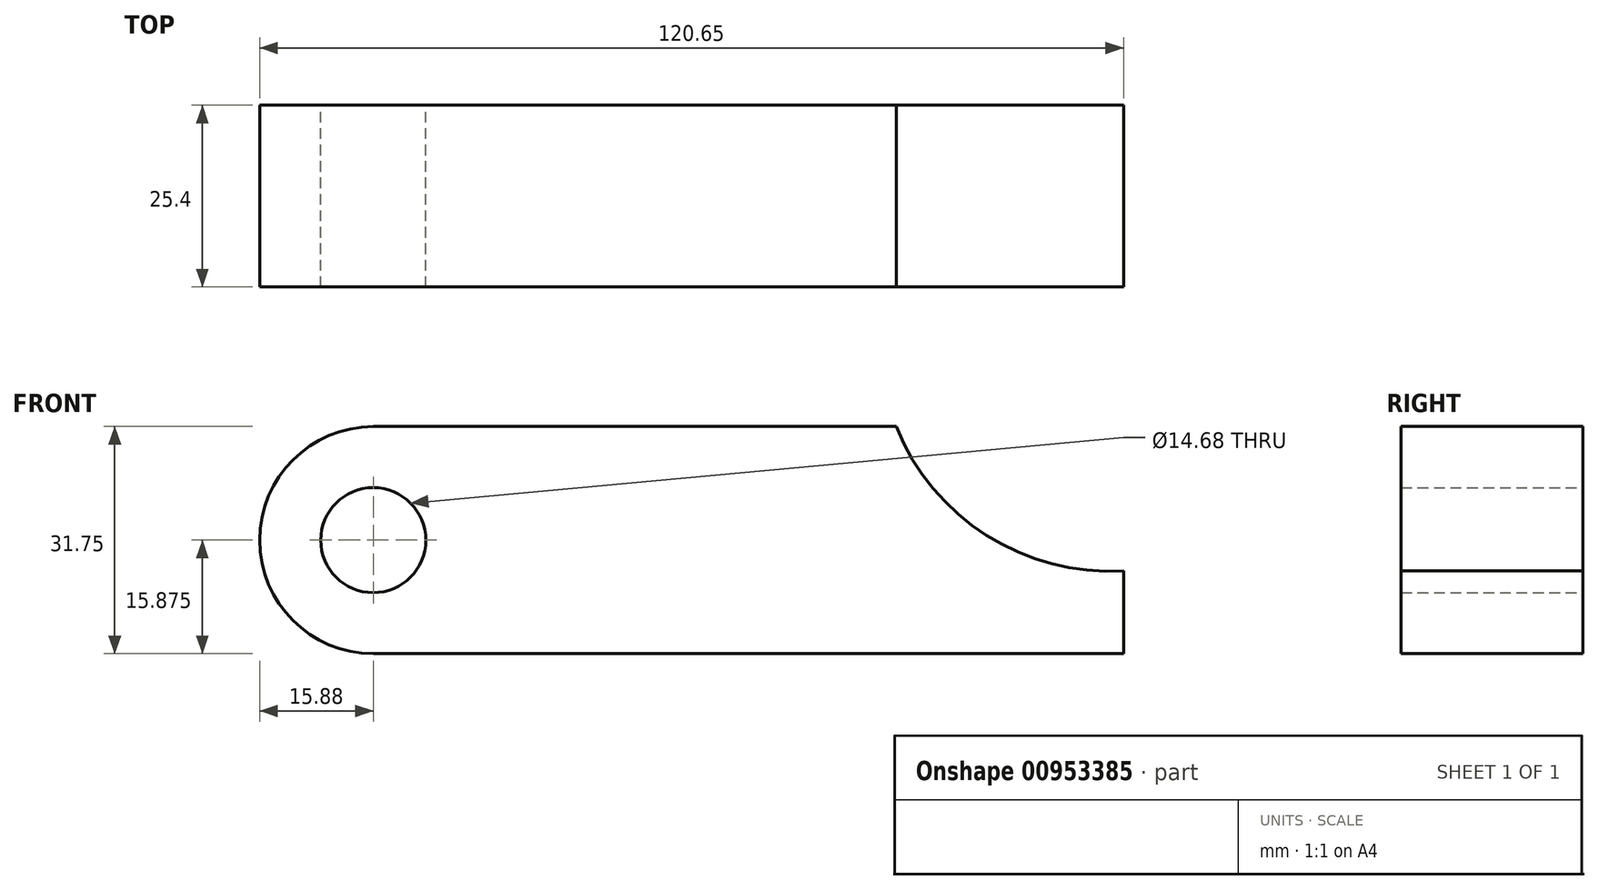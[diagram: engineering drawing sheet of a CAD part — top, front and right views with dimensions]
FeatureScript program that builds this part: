
annotation { "Feature Type Name" : "Feature", "Feature Type Description" : "" }
export const myFeature = defineFeature(function(context is Context, id is Id, definition is map)
    precondition{}
    {
        {
            var Q0;
            Q0=qCreatedBy(makeId("Front.planeOp"),FACE);
            var sketch = newSketch(context, id + "F0", { "sketchPlane" : qUnion([Q0])});
            skLineSegment(sketch, "E0", {"start": v(0, 0) * mm, "end": v(104.78, 0) * mm});
            skLineSegment(sketch, "E1", {"start": v(0, 0) * mm, "end": v(0, 31.75) * mm});
            skLineSegment(sketch, "E2", {"start": v(0, 31.75) * mm, "end": v(73.03, 31.75) * mm});
            skLineSegment(sketch, "E3", {"start": v(104.78, 11.57) * mm, "end": v(104.78, 0) * mm});
            skArc(sketch, "E4", {"start": v(73.03, 31.75) * mm, "mid": v(85.66, 16.56) * mm, "end": v(104.78, 11.57) * mm});
            skArc(sketch, "E5", {"start": v(0, 31.75) * mm, "mid": v(-15.87, 15.87) * mm, "end": v(0, 0) * mm});
            skCircle(sketch, "E6", {"center": v(0, 15.88) * mm, "radius": 7.34 * mm});
            skLineSegment(sketch, "E7", {"start": v(-15.87, 15.88) * mm, "end": v(14.9, 15.88) * mm});
            skSolve(sketch);
        }
        {
            var Q0;
            {var subQ5=sQuery(id+"F0.wireOp",EDGE,"E0");Q0=makeQuery(id+"F0.imprint","IMPRINT",FACE,{"disambiguationData":[TD([[makeQuery(id+"F0.imprint","IMPRINT",EDGE,{"derivedFrom":subQ5}),1.0]])]});}
            var Q1;
            {var subQ1=sQuery(id+"F0.wireOp",EDGE,"E1");var subQ3=sQuery(id+"F0.wireOp",EDGE,"E6");var subQ4=makeQuery(id+"F0.imprint","INTERSECT",VERTEX,{"disambiguationData":[OD(1.0)],"derivedFrom":[subQ1,subQ3]});Q1=makeQuery(id+"F0.imprint","IMPRINT",FACE,{"disambiguationData":[TD([[makeQuery(id+"F0.imprint","IMPRINT",EDGE,{"disambiguationData":[TD([[subQ4,-1.0]])],"derivedFrom":subQ3}),-1.0]])]});}
            var Q2;
            {var subQ1=sQuery(id+"F0.wireOp",EDGE,"E1");var subQ3=sQuery(id+"F0.wireOp",EDGE,"E6");var subQ4=makeQuery(id+"F0.imprint","INTERSECT",VERTEX,{"disambiguationData":[OD(0.0)],"derivedFrom":[subQ1,subQ3]});Q2=makeQuery(id+"F0.imprint","IMPRINT",FACE,{"disambiguationData":[TD([[makeQuery(id+"F0.imprint","IMPRINT",EDGE,{"disambiguationData":[TD([[subQ4,1.0]])],"derivedFrom":subQ3}),-1.0]])]});}
            extrude(context, id + "F1", {"entities" : qUnion([Q0, Q1, Q2]), "depth" : 25.4 * mm, "offsetDistance" : 25.4 * mm});
        }
    });
